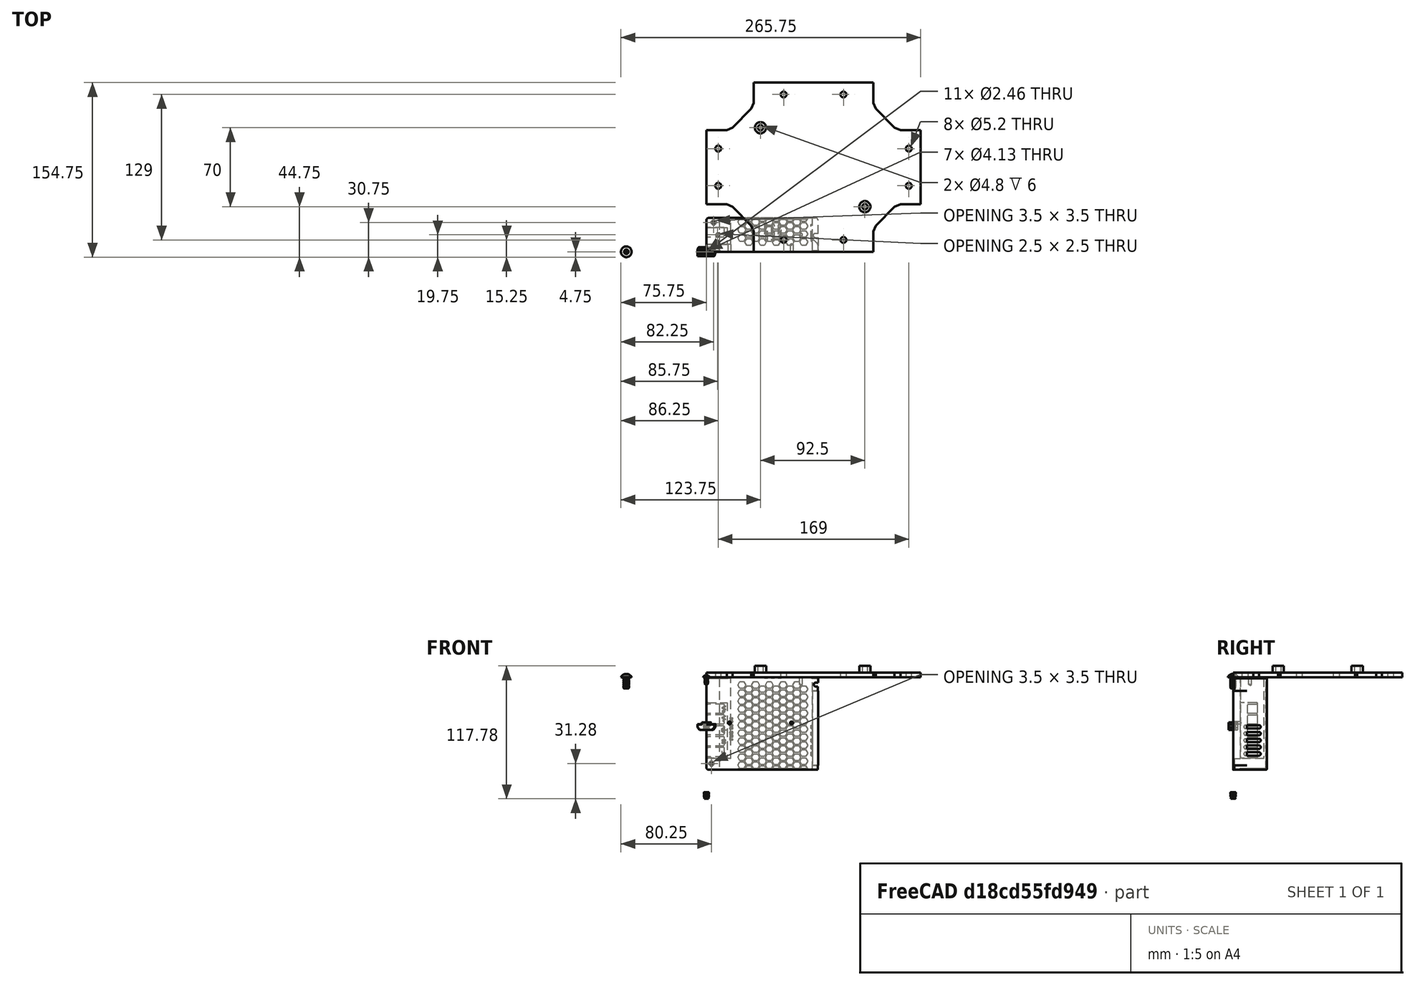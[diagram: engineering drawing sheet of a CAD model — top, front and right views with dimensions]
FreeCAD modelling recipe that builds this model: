
FCSTD DOCUMENT  (FreeCAD 1.0R39109 (Git))
Label: psu-mount
License: All rights reserved
objects: App::Link×14, App::FeaturePython×14, Part::FeaturePython×4, Sketcher::SketchObject×2, PartDesign::Pad×2, PartDesign::Chamfer×1, PartDesign::Body×1, Part::Feature×1, Assembly::JointGroup×1, Assembly::AssemblyObject×1
note: 19 computed .brp shape members not serialized (recipe doc carries the construction recipe); baked Part::Feature solids carry a one-line shape summary decoded from their .brp

FEATURE [Sketcher::SketchObject] Sketch
  ArcFitTolerance = 1e-06
  AttachmentSupport = -> [XY_Plane]
  FullyConstrained = true
  MakeInternals = false
  MapMode = 5
  sketch-geometry (56):
    g0: LineSegment [constr] StartX=0 StartY=0 StartZ=0 EndX=190 EndY=0 EndZ=0
    g1: LineSegment [constr] StartX=190 StartY=0 StartZ=0 EndX=190 EndY=150 EndZ=0
    g2: LineSegment [constr] StartX=190 StartY=150 StartZ=0 EndX=0 EndY=150 EndZ=0
    g3: LineSegment [constr] StartX=0 StartY=150 StartZ=0 EndX=0 EndY=0 EndZ=0
    g4: LineSegment [constr] StartX=0 StartY=0 StartZ=0 EndX=42 EndY=0 EndZ=0
    g5: LineSegment [constr] StartX=42 StartY=0 StartZ=0 EndX=42 EndY=42 EndZ=0
    g6: LineSegment [constr] StartX=42 StartY=42 StartZ=0 EndX=0 EndY=42 EndZ=0
    g7: LineSegment [constr] StartX=0 StartY=42 StartZ=0 EndX=0 EndY=0 EndZ=0
    g8: LineSegment [constr] StartX=0 StartY=150 StartZ=0 EndX=0 EndY=108 EndZ=0
    g9: LineSegment [constr] StartX=0 StartY=108 StartZ=0 EndX=42 EndY=108 EndZ=0
    g10: LineSegment [constr] StartX=42 StartY=108 StartZ=0 EndX=42 EndY=150 EndZ=0
    g11: LineSegment [constr] StartX=42 StartY=150 StartZ=0 EndX=0 EndY=150 EndZ=0
    g12: LineSegment [constr] StartX=190 StartY=150 StartZ=0 EndX=148 EndY=150 EndZ=0
    g13: LineSegment [constr] StartX=148 StartY=150 StartZ=0 EndX=148 EndY=108 EndZ=0
    g14: LineSegment [constr] StartX=148 StartY=108 StartZ=0 EndX=190 EndY=108 EndZ=0
    g15: LineSegment [constr] StartX=190 StartY=108 StartZ=0 EndX=190 EndY=150 EndZ=0
    g16: LineSegment [constr] StartX=190 StartY=0 StartZ=0 EndX=190 EndY=42 EndZ=0
    g17: LineSegment [constr] StartX=190 StartY=42 StartZ=0 EndX=148 EndY=42 EndZ=0
    g18: LineSegment [constr] StartX=148 StartY=42 StartZ=0 EndX=148 EndY=0 EndZ=0
    g19: LineSegment [constr] StartX=148 StartY=0 StartZ=0 EndX=190 EndY=0 EndZ=0
    g20: LineSegment StartX=42 StartY=129 StartZ=0 EndX=21 EndY=108 EndZ=0
    g21: LineSegment StartX=21 StartY=108 StartZ=0 EndX=0 EndY=108 EndZ=0
    g22: LineSegment StartX=0 StartY=108 StartZ=0 EndX=0 EndY=42 EndZ=0
    g23: LineSegment StartX=0 StartY=42 StartZ=0 EndX=21 EndY=42 EndZ=0
    g24: LineSegment StartX=21 StartY=42 StartZ=0 EndX=42 EndY=21 EndZ=0
    g25: LineSegment StartX=42 StartY=21 StartZ=0 EndX=42 EndY=0 EndZ=0
    g26: LineSegment StartX=42 StartY=0 StartZ=0 EndX=148 EndY=0 EndZ=0
    g27: LineSegment StartX=148 StartY=0 StartZ=0 EndX=148 EndY=21 EndZ=0
    g28: LineSegment StartX=148 StartY=21 StartZ=0 EndX=169 EndY=42 EndZ=0
    g29: LineSegment StartX=169 StartY=42 StartZ=0 EndX=190 EndY=42 EndZ=0
    g30: LineSegment StartX=190 StartY=42 StartZ=0 EndX=190 EndY=108 EndZ=0
    g31: LineSegment StartX=190 StartY=108 StartZ=0 EndX=169 EndY=108 EndZ=0
    g32: LineSegment StartX=169 StartY=108 StartZ=0 EndX=148 EndY=129 EndZ=0
    g33: LineSegment StartX=148 StartY=129 StartZ=0 EndX=148 EndY=150 EndZ=0
    g34: LineSegment StartX=148 StartY=150 StartZ=0 EndX=42 EndY=150 EndZ=0
    g35: LineSegment StartX=42 StartY=150 StartZ=0 EndX=42 EndY=129 EndZ=0
    g36: LineSegment [constr] StartX=95 StartY=129 StartZ=0 EndX=95 EndY=150 EndZ=0
    g37: LineSegment [constr] StartX=95 StartY=139.5 StartZ=0 EndX=42 EndY=139.5 EndZ=0
    g38: Circle CenterX=68.5 CenterY=139.5 CenterZ=0 NormalX=0 NormalY=0 NormalZ=1 AngleXU=0 Radius=2.6
    g39: LineSegment [constr] StartX=95 StartY=139.5 StartZ=0 EndX=148 EndY=139.5 EndZ=0
    g40: Circle CenterX=121.5 CenterY=139.5 CenterZ=0 NormalX=0 NormalY=0 NormalZ=1 AngleXU=0 Radius=2.6
    g41: LineSegment [constr] StartX=0 StartY=75 StartZ=0 EndX=21 EndY=75 EndZ=0
    g42: LineSegment [constr] StartX=10.5 StartY=75 StartZ=0 EndX=10.5 EndY=108 EndZ=0
    g43: LineSegment [constr] StartX=10.5 StartY=75 StartZ=0 EndX=10.5 EndY=42 EndZ=0
    g44: Circle CenterX=10.5 CenterY=91.5 CenterZ=0 NormalX=0 NormalY=0 NormalZ=1 AngleXU=0 Radius=2.6
    g45: Circle CenterX=10.5 CenterY=58.5 CenterZ=0 NormalX=0 NormalY=0 NormalZ=1 AngleXU=0 Radius=2.6
    g46: LineSegment [constr] StartX=95 StartY=21 StartZ=0 EndX=95 EndY=0 EndZ=0
    g47: LineSegment [constr] StartX=95 StartY=10.5 StartZ=0 EndX=42 EndY=10.5 EndZ=0
    g48: LineSegment [constr] StartX=95 StartY=10.5 StartZ=0 EndX=148 EndY=10.5 EndZ=0
    g49: Circle CenterX=68.5 CenterY=10.5 CenterZ=0 NormalX=0 NormalY=0 NormalZ=1 AngleXU=0 Radius=2.6
    g50: Circle CenterX=121.5 CenterY=10.5 CenterZ=0 NormalX=0 NormalY=0 NormalZ=1 AngleXU=0 Radius=2.6
    g51: LineSegment [constr] StartX=169 StartY=75 StartZ=0 EndX=190 EndY=75 EndZ=0
    g52: LineSegment [constr] StartX=179.5 StartY=75 StartZ=0 EndX=179.5 EndY=42 EndZ=0
    g53: LineSegment [constr] StartX=179.5 StartY=75 StartZ=0 EndX=179.5 EndY=108 EndZ=0
    g54: Circle CenterX=179.5 CenterY=91.5 CenterZ=0 NormalX=0 NormalY=0 NormalZ=1 AngleXU=0 Radius=2.6
    g55: Circle CenterX=179.5 CenterY=58.5 CenterZ=0 NormalX=0 NormalY=0 NormalZ=1 AngleXU=0 Radius=2.6
  constraints (127):
    c: Coincident(g0,g1)
    c: Coincident(g1,g2)
    c: Coincident(g2,g3)
    c: Coincident(g3,g0)
    c: Horizontal(g0)
    c: Horizontal(g2)
    c: Vertical(g1)
    c: Vertical(g3)
    c: Distance(g1,g3) = 190
    c: Distance(g0,g2) = 150
    c: Coincident(g0,g-1)
    c: Coincident(g4,g5)
    c: Coincident(g5,g6)
    c: Coincident(g6,g7)
    c: Coincident(g7,g4)
    c: Horizontal(g4)
    c: Horizontal(g6)
    c: Vertical(g5)
    c: Vertical(g7)
    c: Distance(g5,g7) = 42
    c: Distance(g4,g6) = 42
    c: Coincident(g4,g0)
    c: Coincident(g8,g9)
    c: Coincident(g9,g10)
    c: Coincident(g10,g11)
    c: Coincident(g11,g8)
    c: Vertical(g8)
    c: Vertical(g10)
    c: Horizontal(g9)
    c: Horizontal(g11)
    c: Distance(g8,g10) = 42
    c: Distance(g9,g11) = 42
    c: Coincident(g8,g2)
    c: Coincident(g12,g13)
    c: Coincident(g13,g14)
    c: Coincident(g14,g15)
    c: Coincident(g15,g12)
    c: Horizontal(g12)
    c: Horizontal(g14)
    c: Vertical(g13)
    c: Vertical(g15)
    c: Distance(g13,g15) = 42
    c: Distance(g12,g14) = 42
    c: Coincident(g12,g1)
    c: Coincident(g16,g17)
    c: Coincident(g17,g18)
    c: Coincident(g18,g19)
    c: Coincident(g19,g16)
    c: Vertical(g16)
    c: Vertical(g18)
    c: Horizontal(g17)
    c: Horizontal(g19)
    c: Distance(g16,g18) = 42
    c: Distance(g17,g19) = 42
    c: Coincident(g16,g0)
    c: Symmetric(g10,g10,g20)
    c: Symmetric(g9,g9,g20)
    c: Coincident(g21,g20)
    c: Coincident(g21,g8)
    c: Coincident(g22,g8)
    c: Coincident(g22,g6)
    c: Coincident(g23,g6)
    c: Symmetric(g6,g6,g23)
    c: Coincident(g24,g23)
    c: Symmetric(g5,g5,g24)
    c: Coincident(g25,g24)
    c: Coincident(g25,g4)
    c: Coincident(g26,g4)
    c: Coincident(g26,g18)
    c: Coincident(g27,g18)
    c: Symmetric(g18,g18,g27)
    c: Coincident(g28,g27)
    c: Symmetric(g17,g17,g28)
    c: Coincident(g29,g28)
    c: Coincident(g29,g16)
    c: Coincident(g30,g16)
    c: Coincident(g30,g14)
    c: Coincident(g31,g14)
    c: Symmetric(g14,g14,g31)
    c: Coincident(g32,g31)
    c: Symmetric(g13,g13,g32)
    c: Coincident(g33,g32)
    c: Coincident(g33,g12)
    c: Coincident(g34,g12)
    c: Coincident(g34,g10)
    c: Coincident(g35,g10)
    c: Coincident(g35,g20)
    c: Symmetric(g20,g32,g36)
    c: Symmetric(g34,g34,g36)
    c: Symmetric(g36,g36,g37)
    c: Symmetric(g35,g35,g37)
    c: Diameter(g38) = 5.2
    c: Symmetric(g37,g37,g38)
    c: Coincident(g39,g37)
    c: Symmetric(g33,g33,g39)
    c: Diameter(g40) = 5.2
    c: Symmetric(g39,g39,g40)
    c: Symmetric(g22,g22,g41)
    c: Symmetric(g20,g23,g41)
    c: Symmetric(g41,g41,g42)
    c: Symmetric(g21,g21,g42)
    c: Coincident(g43,g42)
    c: Symmetric(g23,g23,g43)
    c: Diameter(g44) = 5.2
    c: Symmetric(g42,g42,g44)
    c: Diameter(g45) = 5.2
    c: Symmetric(g43,g43,g45)
    c: Symmetric(g24,g27,g46)
    c: Symmetric(g26,g26,g46)
    c: Symmetric(g46,g46,g47)
    c: Symmetric(g25,g25,g47)
    c: Coincident(g48,g47)
    c: Symmetric(g27,g27,g48)
    c: Diameter(g49) = 5.2
    c: Symmetric(g47,g47,g49)
    c: Diameter(g50) = 5.2
    c: Symmetric(g48,g48,g50)
    c: Symmetric(g31,g28,g51)
    c: Symmetric(g30,g30,g51)
    c: Symmetric(g51,g51,g52)
    c: Symmetric(g29,g29,g52)
    c: Coincident(g53,g52)
    c: Symmetric(g31,g31,g53)
    c: Diameter(g54) = 5.2
    c: Symmetric(g53,g53,g54)
    c: Diameter(g55) = 5.2
    c: Symmetric(g52,g52,g55)
FEATURE [PartDesign::Pad] Pad
  Direction = (0,0,1)
  Length = 4
  Length2 = 10
  Profile = -> Sketch
  ReferenceAxis = -> Sketch [N_Axis]
  Refine = true
  Suppressed = false
  Type = 0
FEATURE [PartDesign::Chamfer] Chamfer
  Angle = 45
  Base = -> Pad [Edge1,Edge2,Edge11,Edge14,Edge23,Edge26,Edge38,Edge35]
  BaseFeature = -> Pad
  ChamferType = 0
  FlipDirection = false
  Refine = true
  Size = 3
  Size2 = 1
  SupportTransform = false
  Suppressed = false
  UseAllEdges = false
FEATURE [Sketcher::SketchObject] Sketch001
  ArcFitTolerance = 1e-06
  AttachmentSupport = -> [Chamfer]
  FullyConstrained = true
  MakeInternals = false
  MapMode = 5
  Placement = pos=(0,0,4) rot=(0,0,1;0rad)
  sketch-geometry (16):
    g0: LineSegment [constr] StartX=0 StartY=0 StartZ=0 EndX=190 EndY=0 EndZ=0
    g1: LineSegment [constr] StartX=190 StartY=0 StartZ=0 EndX=190 EndY=150 EndZ=0
    g2: LineSegment [constr] StartX=190 StartY=150 StartZ=0 EndX=0 EndY=150 EndZ=0
    g3: LineSegment [constr] StartX=0 StartY=150 StartZ=0 EndX=0 EndY=0 EndZ=0
    g4: LineSegment [constr] StartX=0 StartY=150 StartZ=0 EndX=0 EndY=110 EndZ=0
    g5: LineSegment [constr] StartX=0 StartY=110 StartZ=0 EndX=48 EndY=110 EndZ=0
    g6: LineSegment [constr] StartX=48 StartY=110 StartZ=0 EndX=48 EndY=150 EndZ=0
    g7: LineSegment [constr] StartX=48 StartY=150 StartZ=0 EndX=0 EndY=150 EndZ=0
    g8: Circle CenterX=48 CenterY=110 CenterZ=0 NormalX=0 NormalY=0 NormalZ=1 AngleXU=0 Radius=5
    g9: Circle CenterX=48 CenterY=110 CenterZ=0 NormalX=0 NormalY=0 NormalZ=1 AngleXU=0 Radius=2.4
    g10: LineSegment [constr] StartX=48 StartY=110 StartZ=0 EndX=48 EndY=40 EndZ=0
    g11: LineSegment [constr] StartX=48 StartY=40 StartZ=0 EndX=140.5 EndY=40 EndZ=0
    g12: LineSegment [constr] StartX=140.5 StartY=40 StartZ=0 EndX=140.5 EndY=110 EndZ=0
    g13: LineSegment [constr] StartX=140.5 StartY=110 StartZ=0 EndX=48 EndY=110 EndZ=0
    g14: Circle CenterX=140.5 CenterY=40 CenterZ=0 NormalX=0 NormalY=0 NormalZ=1 AngleXU=0 Radius=2.4
    g15: Circle CenterX=140.5 CenterY=40 CenterZ=0 NormalX=0 NormalY=0 NormalZ=1 AngleXU=0 Radius=5
  constraints (41):
    c: Coincident(g0,g1)
    c: Coincident(g1,g2)
    c: Coincident(g2,g3)
    c: Coincident(g3,g0)
    c: Horizontal(g0)
    c: Horizontal(g2)
    c: Vertical(g1)
    c: Vertical(g3)
    c: Distance(g1,g3) = 190
    c: Distance(g0,g2) = 150
    c: Coincident(g0,g-1)
    c: Coincident(g4,g5)
    c: Coincident(g5,g6)
    c: Coincident(g6,g7)
    c: Coincident(g7,g4)
    c: Vertical(g4)
    c: Vertical(g6)
    c: Horizontal(g5)
    c: Horizontal(g7)
    c: Distance(g4,g6) = 48
    c: Distance(g5,g7) = 40
    c: Coincident(g4,g2)
    c: Diameter(g8) = 10
    c: Coincident(g8,g5)
    c: Diameter(g9) = 4.8
    c: Coincident(g9,g5)
    c: Coincident(g10,g11)
    c: Coincident(g11,g12)
    c: Coincident(g12,g13)
    c: Coincident(g13,g10)
    c: Vertical(g10)
    c: Vertical(g12)
    c: Horizontal(g11)
    c: Horizontal(g13)
    c: Distance(g10,g12) = 92.5
    c: Distance(g11,g13) = 70
    c: Coincident(g10,g5)
    c: Diameter(g14) = 4.8
    c: Coincident(g14,g11)
    c: Diameter(g15) = 10
    c: Coincident(g15,g11)
FEATURE [PartDesign::Pad] Pad001
  BaseFeature = -> Chamfer
  Direction = (0,0,1)
  Length = 6
  Length2 = 10
  Profile = -> Sketch001
  ReferenceAxis = -> Sketch001 [N_Axis]
  Refine = true
  Suppressed = false
  Type = 0
FEATURE [PartDesign::Body] Body  label="mount"
  AllowCompound = false
  Group = -> [Sketch,Pad,Chamfer,Sketch001,Pad001]
  Origin = -> Origin
  Tip = -> Pad001
FEATURE [Part::FeaturePython] Screw  label="M5x10-Screw"  # WARN: FeaturePython — macro-defined, semantics opaque (R4)
  Diameter = 3
  Invert = false
  LeftHanded = false
  Length = 1
  LengthCustom = 10
  MatchOuter = false
  OffsetAngle = 0
  Placement = pos=(-71,0,0) rot=(0,0,1;0rad)
  Thread = true
  Type = 85
FEATURE [Part::FeaturePython] TSlot  label="M5 x 30/40 series-TSlot"  # WARN: FeaturePython — macro-defined, semantics opaque (R4)
  Diameter = 3
  Invert = false
  LeftHanded = false
  MatchOuter = false
  OffsetAngle = 0
  Placement = pos=(0,0,-40) rot=(0,0,1;0rad)
  SlotWidth = 1
  Thread = true
  Type = 1
FEATURE [Part::FeaturePython] Insert  label="M3x5.74-Insert"  # WARN: FeaturePython — macro-defined, semantics opaque (R4)
  Diameter = 3
  ExternalDiam = 4.55
  Invert = false
  LeftHanded = false
  Length = 5.74
  MatchOuter = false
  OffsetAngle = 0
  Placement = pos=(0,0,-102) rot=(0,0,1;0rad)
  Thread = true
  Type = 0
FEATURE [App::Link] mount  label="mount001"
  LinkedObject = -> Body
FEATURE [App::Link] M3x5_74_Insert  label="M3x5.74-Insert001"
  LinkPlacement = pos=(48,110,10.0967) rot=(0,0,1;0rad)
  LinkedObject = -> Insert
  Placement = pos=(48,110,10.0967) rot=(0,0,1;0rad)
FEATURE [App::Link] M3x5_74_Insert001  label="M3x5.74-Insert002"
  LinkPlacement = pos=(140.5,40,10.0967) rot=(0,0,1;0rad)
  LinkedObject = -> Insert
  Placement = pos=(140.5,40,10.0967) rot=(0,0,1;0rad)
FEATURE [App::FeaturePython] GroundedJoint  # Assembly grounded joint (typed FeaturePython)
  ObjectToGround = -> mount
FEATURE [App::FeaturePython] Joint  label="Fixed"  # Assembly joint (typed FeaturePython)
  Activated = true
  AngleMax = 0
  AngleMin = 0
  Detach1 = false
  Detach2 = false
  Distance = 0
  Distance2 = 0
  EnableAngleMax = false
  EnableAngleMin = false
  EnableLengthMax = false
  EnableLengthMin = false
  JointType = 0 (Fixed)
  LengthMax = 0
  LengthMin = 0
  Offset2 = pos=(0,0,-5) rot=(0,0,1;0rad)
  Placement1 = pos=(0,0,-5.09667) rot=(0,0,1;0rad)
  Placement2 = pos=(140.5,40,5) rot=(0,0,1;0rad)
  Reference1 = -> Assembly [M3x5_74_Insert001.Edge298,M3x5_74_Insert001.Edge298]
  Reference2 = -> Assembly [mount.Edge103,mount.Edge103]
FEATURE [App::FeaturePython] Joint001  label="Fixed001"  # Assembly joint (typed FeaturePython)
  Activated = true
  AngleMax = 0
  AngleMin = 0
  Detach1 = false
  Detach2 = false
  Distance = 0
  Distance2 = 0
  EnableAngleMax = false
  EnableAngleMin = false
  EnableLengthMax = false
  EnableLengthMin = false
  JointType = 0 (Fixed)
  LengthMax = 0
  LengthMin = 0
  Offset2 = pos=(0,0,-5) rot=(0,0,1;0rad)
  Placement1 = pos=(0,0,-5.09667) rot=(0,0,1;0rad)
  Placement2 = pos=(48,110,5) rot=(0,0,1;0rad)
  Reference1 = -> Assembly [M3x5_74_Insert.Edge298,M3x5_74_Insert.Edge298]
  Reference2 = -> Assembly [mount.Edge104,mount.Edge104]
FEATURE [App::Link] M5x10_Screw  label="M5x10-Screw001"
  LinkPlacement = pos=(68.5,10.5,0) rot=(1,0,0;3.14159rad)
  LinkedObject = -> Screw
  Placement = pos=(68.5,10.5,0) rot=(1,0,0;3.14159rad)
FEATURE [App::FeaturePython] Joint002  label="Fixed002"  # Assembly joint (typed FeaturePython)
  Activated = true
  AngleMax = 0
  AngleMin = 0
  Detach1 = false
  Detach2 = false
  Distance = 0
  Distance2 = 0
  EnableAngleMax = false
  EnableAngleMin = false
  EnableLengthMax = false
  EnableLengthMin = false
  JointType = 0 (Fixed)
  LengthMax = 0
  LengthMin = 0
  Placement2 = pos=(68.5,10.5,0) rot=(0,0,1;0rad)
  Reference1 = -> Assembly [M5x10_Screw.Edge5,M5x10_Screw.Edge5]
  Reference2 = -> Assembly [mount.Edge35,mount.Edge35]
FEATURE [App::Link] M5x10_Screw002  label="M5x10-Screw003"
  LinkPlacement = pos=(179.5,58.5,0) rot=(1,0,0;3.14159rad)
  LinkedObject = -> Screw
  Placement = pos=(179.5,58.5,0) rot=(1,0,0;3.14159rad)
FEATURE [App::Link] M5x10_Screw003  label="M5x10-Screw004"
  LinkPlacement = pos=(179.5,91.5,0) rot=(1,0,0;3.14159rad)
  LinkedObject = -> Screw
  Placement = pos=(179.5,91.5,0) rot=(1,0,0;3.14159rad)
FEATURE [App::Link] M5x10_Screw004  label="M5x10-Screw005"
  LinkPlacement = pos=(121.5,139.5,0) rot=(1,0,0;3.14159rad)
  LinkedObject = -> Screw
  Placement = pos=(121.5,139.5,0) rot=(1,0,0;3.14159rad)
FEATURE [App::Link] M5x10_Screw005  label="M5x10-Screw006"
  LinkPlacement = pos=(68.5,139.5,0) rot=(1,0,0;3.14159rad)
  LinkedObject = -> Screw
  Placement = pos=(68.5,139.5,0) rot=(1,0,0;3.14159rad)
FEATURE [App::Link] M5x10_Screw006  label="M5x10-Screw007"
  LinkPlacement = pos=(10.5,58.5,0) rot=(1,0,0;3.14159rad)
  LinkedObject = -> Screw
  Placement = pos=(10.5,58.5,0) rot=(1,0,0;3.14159rad)
FEATURE [App::FeaturePython] Joint004  label="Fixed004"  # Assembly joint (typed FeaturePython)
  Activated = true
  AngleMax = 0
  AngleMin = 0
  Detach1 = false
  Detach2 = false
  Distance = 0
  Distance2 = 0
  EnableAngleMax = false
  EnableAngleMin = false
  EnableLengthMax = false
  EnableLengthMin = false
  JointType = 0 (Fixed)
  LengthMax = 0
  LengthMin = 0
  Placement2 = pos=(179.5,58.5,0) rot=(0,0,1;0rad)
  Reference1 = -> Assembly [M5x10_Screw002.Edge5,M5x10_Screw002.Edge5]
  Reference2 = -> Assembly [mount.Edge30,mount.Edge30]
FEATURE [App::FeaturePython] Joint005  label="Fixed005"  # Assembly joint (typed FeaturePython)
  Activated = true
  AngleMax = 0
  AngleMin = 0
  Detach1 = false
  Detach2 = false
  Distance = 0
  Distance2 = 0
  EnableAngleMax = false
  EnableAngleMin = false
  EnableLengthMax = false
  EnableLengthMin = false
  JointType = 0 (Fixed)
  LengthMax = 0
  LengthMin = 0
  Placement2 = pos=(179.5,91.5,0) rot=(0,0,1;0rad)
  Reference1 = -> Assembly [M5x10_Screw003.Edge5,M5x10_Screw003.Edge5]
  Reference2 = -> Assembly [mount.Edge28,mount.Edge28]
FEATURE [App::FeaturePython] Joint006  label="Fixed006"  # Assembly joint (typed FeaturePython)
  Activated = true
  AngleMax = 0
  AngleMin = 0
  Detach1 = false
  Detach2 = false
  Distance = 0
  Distance2 = 0
  EnableAngleMax = false
  EnableAngleMin = false
  EnableLengthMax = false
  EnableLengthMin = false
  JointType = 0 (Fixed)
  LengthMax = 0
  LengthMin = 0
  Placement2 = pos=(121.5,139.5,0) rot=(0,0,1;0rad)
  Reference1 = -> Assembly [M5x10_Screw004.Edge5,M5x10_Screw004.Edge5]
  Reference2 = -> Assembly [mount.Edge31,mount.Edge31]
FEATURE [App::FeaturePython] Joint007  label="Fixed007"  # Assembly joint (typed FeaturePython)
  Activated = true
  AngleMax = 0
  AngleMin = 0
  Detach1 = false
  Detach2 = false
  Distance = 0
  Distance2 = 0
  EnableAngleMax = false
  EnableAngleMin = false
  EnableLengthMax = false
  EnableLengthMin = false
  JointType = 0 (Fixed)
  LengthMax = 0
  LengthMin = 0
  Placement2 = pos=(68.5,139.5,0) rot=(0,0,1;0rad)
  Reference1 = -> Assembly [M5x10_Screw005.Edge5,M5x10_Screw005.Edge5]
  Reference2 = -> Assembly [mount.Edge32,mount.Edge32]
FEATURE [App::FeaturePython] Joint008  label="Fixed008"  # Assembly joint (typed FeaturePython)
  Activated = true
  AngleMax = 0
  AngleMin = 0
  Detach1 = false
  Detach2 = false
  Distance = 0
  Distance2 = 0
  EnableAngleMax = false
  EnableAngleMin = false
  EnableLengthMax = false
  EnableLengthMin = false
  JointType = 0 (Fixed)
  LengthMax = 0
  LengthMin = 0
  Placement2 = pos=(10.5,58.5,0) rot=(0,0,1;0rad)
  Reference1 = -> Assembly [M5x10_Screw006.Edge5,M5x10_Screw006.Edge5]
  Reference2 = -> Assembly [mount.Edge33,mount.Edge33]
FEATURE [App::Link] M5x10_Screw007  label="M5x10-Screw008"
  LinkPlacement = pos=(10.5,91.5,0) rot=(1,0,0;3.14159rad)
  LinkedObject = -> Screw
  Placement = pos=(10.5,91.5,0) rot=(1,0,0;3.14159rad)
FEATURE [App::FeaturePython] Joint009  label="Fixed009"  # Assembly joint (typed FeaturePython)
  Activated = true
  AngleMax = 0
  AngleMin = 0
  Detach1 = false
  Detach2 = false
  Distance = 0
  Distance2 = 0
  EnableAngleMax = false
  EnableAngleMin = false
  EnableLengthMax = false
  EnableLengthMin = false
  JointType = 0 (Fixed)
  LengthMax = 0
  LengthMin = 0
  Placement2 = pos=(10.5,91.5,0) rot=(0,0,1;0rad)
  Reference1 = -> Assembly [M5x10_Screw007.Edge5,M5x10_Screw007.Edge5]
  Reference2 = -> Assembly [mount.Edge29,mount.Edge29]
FEATURE [App::Link] M5x10_Screw008  label="M5x10-Screw009"
  LinkPlacement = pos=(121.5,10.5,0) rot=(1,0,0;3.14159rad)
  LinkedObject = -> Screw
  Placement = pos=(121.5,10.5,0) rot=(1,0,0;3.14159rad)
FEATURE [App::FeaturePython] Joint016  label="Fixed016"  # Assembly joint (typed FeaturePython)
  Activated = true
  AngleMax = 0
  AngleMin = 0
  Detach1 = false
  Detach2 = false
  Distance = 0
  Distance2 = 0
  EnableAngleMax = false
  EnableAngleMin = false
  EnableLengthMax = false
  EnableLengthMin = false
  JointType = 0 (Fixed)
  LengthMax = 0
  LengthMin = 0
  Placement2 = pos=(121.5,10.5,0) rot=(0,0,1;0rad)
  Reference1 = -> Assembly [M5x10_Screw008.Edge5,M5x10_Screw008.Edge5]
  Reference2 = -> Assembly [mount.Edge34,mount.Edge34]
FEATURE [Part::Feature] Part__Feature  label="MW LRS-50-24"
  shape: bbox 99 x 30 x 82 mm, 1343 faces (baked)
FEATURE [App::Link] MW_LRS_50_24  label="MW LRS-50-025"
  LinkPlacement = pos=(43.5,33.5,10) rot=(1,0,0;1.5708rad)
  LinkedObject = -> Part__Feature
  Placement = pos=(43.5,33.5,10) rot=(1,0,0;1.5708rad)
FEATURE [App::FeaturePython] Joint019  label="Fixed019"  # Assembly joint (typed FeaturePython)
  Activated = true
  AngleMax = 0
  AngleMin = 0
  Detach1 = false
  Detach2 = false
  Distance = 0
  Distance2 = 0
  EnableAngleMax = false
  EnableAngleMin = false
  EnableLengthMax = false
  EnableLengthMin = false
  JointType = 0 (Fixed)
  LengthMax = 0
  LengthMin = 0
  Offset2 = pos=(0,0,0) rot=(0,0,-1;1.5708rad)
  Placement1 = pos=(4.5,-1.8e-15,-76.5) rot=(-0.57735,-0.57735,-0.57735;2.0944rad)
  Placement2 = pos=(48,110,10) rot=(0,0,-1;1.5708rad)
  Reference1 = -> Assembly [MW_LRS_50_24.Edge1250,MW_LRS_50_24.Edge1250]
  Reference2 = -> Assembly [mount.Edge104,mount.Edge104]
FEATURE [Part::FeaturePython] Screw001  label="M3x6-Screw"  # WARN: FeaturePython — macro-defined, semantics opaque (R4)
  Diameter = 1
  Invert = false
  LeftHanded = false
  Length = 9
  LengthCustom = 6
  MatchOuter = false
  OffsetAngle = 0
  Thread = true
  Type = 85
FEATURE [App::Link] M3x6_Screw  label="M3x6-Screw001"
  LinkPlacement = pos=(48,110,11) rot=(0,0,1;4.71239rad)
  LinkedObject = -> Screw001
  Placement = pos=(48,110,11) rot=(0,0,1;4.71239rad)
FEATURE [App::FeaturePython] Joint020  label="Fixed020"  # Assembly joint (typed FeaturePython)
  Activated = true
  AngleMax = 0
  AngleMin = 0
  Detach1 = false
  Detach2 = false
  Distance = 0
  Distance2 = 0
  EnableAngleMax = false
  EnableAngleMin = false
  EnableLengthMax = false
  EnableLengthMin = false
  JointType = 0 (Fixed)
  LengthMax = 0
  LengthMin = 0
  Placement2 = pos=(4.5,1,-76.5) rot=(-0.57735,-0.57735,-0.57735;2.0944rad)
  Reference1 = -> Assembly [M3x6_Screw.Edge5,M3x6_Screw.Edge5]
  Reference2 = -> Assembly [MW_LRS_50_24.Edge1313,MW_LRS_50_24.Edge1313]
FEATURE [App::Link] M3x6_Screw001  label="M3x6-Screw002"
  LinkPlacement = pos=(140.5,40,11) rot=(0,0,-1;1.5708rad)
  LinkedObject = -> Screw001
  Placement = pos=(140.5,40,11) rot=(0,0,-1;1.5708rad)
FEATURE [App::FeaturePython] Joint021  label="Revolute021"  # Assembly joint (typed FeaturePython)
  Activated = true
  AngleMax = 0
  AngleMin = 0
  Detach1 = false
  Detach2 = false
  Distance = 0
  Distance2 = 0
  EnableAngleMax = false
  EnableAngleMin = false
  EnableLengthMax = false
  EnableLengthMin = false
  JointType = 1 (Revolute)
  LengthMax = 0
  LengthMin = 0
  Placement2 = pos=(97,1,-6.5) rot=(-0.57735,-0.57735,-0.57735;2.0944rad)
  Reference1 = -> Assembly [M3x6_Screw001.Edge5,M3x6_Screw001.Edge5]
  Reference2 = -> Assembly [MW_LRS_50_24.Edge1311,MW_LRS_50_24.Edge1311]
FEATURE [Assembly::JointGroup] Joints
  Group = -> [GroundedJoint,Joint,Joint001,Joint002,Joint004,Joint005,Joint006,Joint007,Joint008,Joint009,Joint016,Joint019,Joint020,Joint021]
FEATURE [Assembly::AssemblyObject] Assembly  label="psu-mount"
  Group = -> [Joints,mount,M3x5_74_Insert,M3x5_74_Insert001,GroundedJoint,Joint,Joint001,M5x10_Screw,Joint002,M5x10_Screw002,M5x10_Screw003,M5x10_Screw004,M5x10_Screw005,M5x10_Screw006,Joint004,Joint005,Joint006,Joint007,Joint008,M5x10_Screw007,Joint009,M5x10_Screw008,Joint016,MW_LRS_50_24,Joint019,M3x6_Screw,Joint020,M3x6_Screw001,Joint021]
  Origin = -> Origin001
  Type = Assembly
